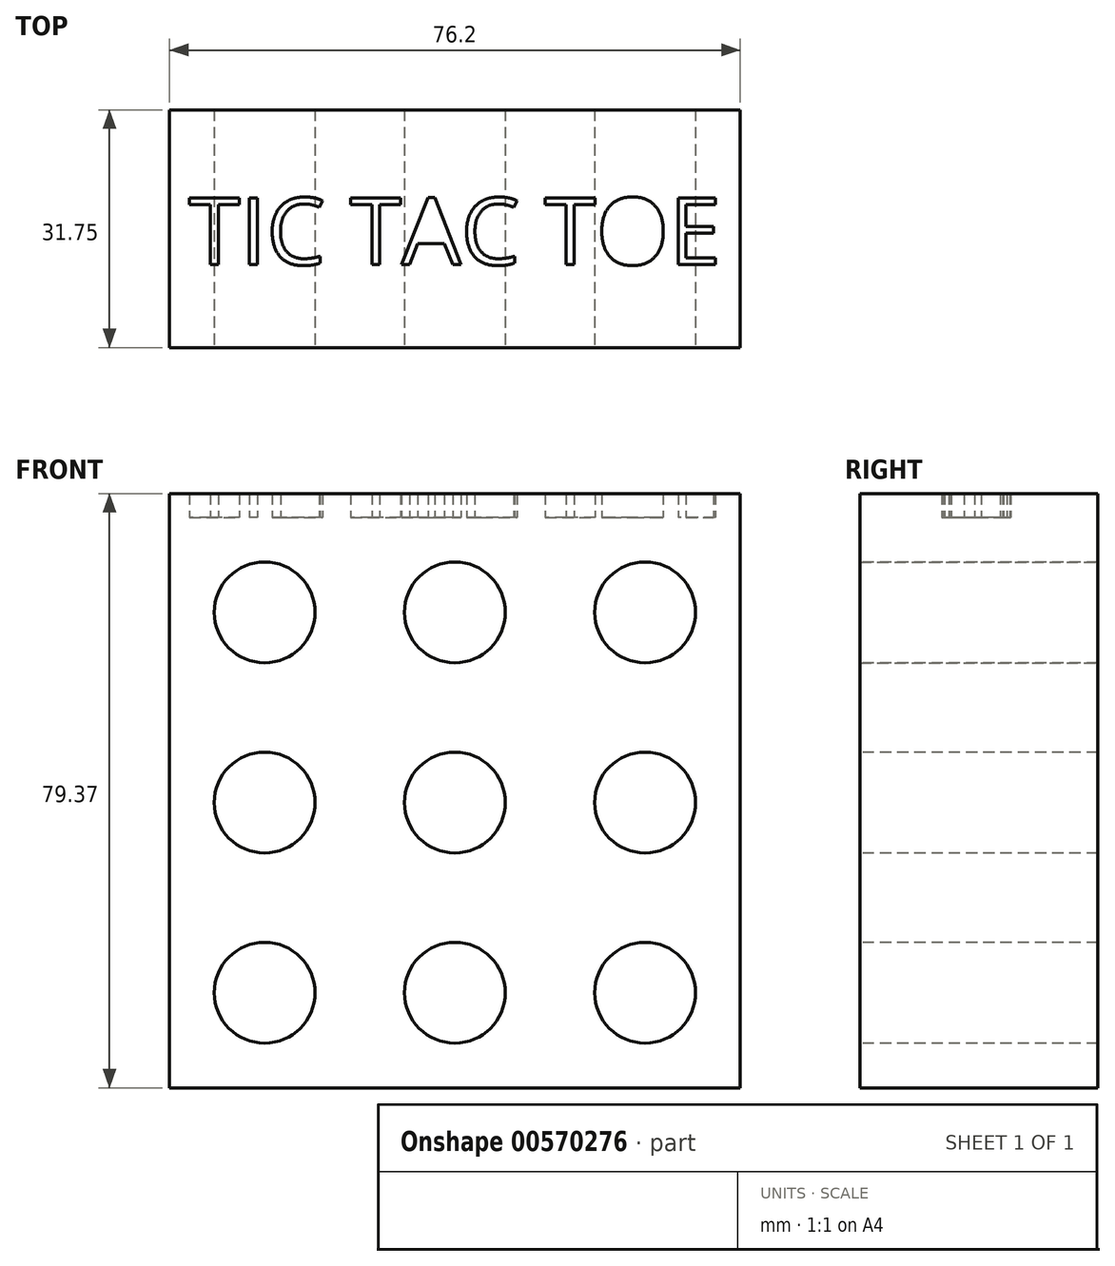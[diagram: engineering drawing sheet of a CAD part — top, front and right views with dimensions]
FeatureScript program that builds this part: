
annotation { "Feature Type Name" : "Feature", "Feature Type Description" : "" }
export const myFeature = defineFeature(function(context is Context, id is Id, definition is map)
    precondition{}
    {
        {
            var Q0;
            Q0=qCreatedBy(makeId("Front.planeOp"),FACE);
            var sketch = newSketch(context, id + "F0", { "sketchPlane" : qUnion([Q0])});
            skLineSegment(sketch, "E0.bottom", {"start": v(-47.47, 51.39) * mm, "end": v(28.73, 51.39) * mm});
            skLineSegment(sketch, "E0.top", {"start": v(-47.47, -24.81) * mm, "end": v(28.73, -24.81) * mm});
            skLineSegment(sketch, "E0.left", {"start": v(-47.47, 51.39) * mm, "end": v(-47.47, -24.81) * mm});
            skLineSegment(sketch, "E0.right", {"start": v(28.73, 51.39) * mm, "end": v(28.73, -24.81) * mm});
            skLineSegment(sketch, "E1", {"start": v(-9.37, 51.39) * mm, "end": v(-9.37, -24.81) * mm, "construction": true});
            skLineSegment(sketch, "E2", {"start": v(-47.47, 13.29) * mm, "end": v(28.73, 13.29) * mm, "construction": true});
            skSolve(sketch);
        }
        {
            var Q0;
            Q0=makeQuery(id+"F0.imprint","IMPRINT",FACE,{"disambiguationData":[TD([[makeQuery(id+"F0.imprint","IMPRINT",EDGE,{"derivedFrom":sQuery(id+"F0.wireOp",EDGE,"E0.bottom")}),-1.0]])]});
            extrude(context, id + "F1", {"entities" : qUnion([Q0]), "depth" : 31.75 * mm, "offsetDistance" : 25.4 * mm});
        }
        {
            var Q0;
            Q0=makeQuery(id+"F1.opExtrude","CAP_FACE",FACE,{"disambiguationData":[OSD([sQuery(id+"F0.wireOp",EDGE,"E0.bottom"),sQuery(id+"F0.wireOp",EDGE,"E0.top"),sQuery(id+"F0.wireOp",EDGE,"E0.left"),sQuery(id+"F0.wireOp",EDGE,"E0.right")])],"isStart":false});
            var sketch = newSketch(context, id + "F2", { "sketchPlane" : qUnion([Q0])});
            skCircle(sketch, "E3", {"center": v(-9.37, 13.29) * mm, "radius": 6.73 * mm});
            skSolve(sketch);
        }
        {
            var Q0;
            Q0=makeQuery(id+"F2.imprint","IMPRINT",FACE,{"disambiguationData":[TD([[makeQuery(id+"F2.imprint","IMPRINT",EDGE,{"derivedFrom":sQuery(id+"F2.wireOp",EDGE,"E3")}),1.0]])]});
            extrude(context, id + "F3", {"entities" : qUnion([Q0]), "operationType" : NewBodyOperationType.REMOVE, "oppositeDirection" : true, "depth" : 50.8 * mm, "offsetDistance" : 25.4 * mm});
        }
        {
            var Q0;
            Q0=makeQuery(id+"F1.opExtrude","CAP_FACE",FACE,{"disambiguationData":[OSD([sQuery(id+"F0.wireOp",EDGE,"E0.bottom"),sQuery(id+"F0.wireOp",EDGE,"E0.top"),sQuery(id+"F0.wireOp",EDGE,"E0.left"),sQuery(id+"F0.wireOp",EDGE,"E0.right")])],"isStart":false});
            var sketch = newSketch(context, id + "F4", { "sketchPlane" : qUnion([Q0])});
            skCircle(sketch, "E4", {"center": v(16.03, 38.69) * mm, "radius": 6.73 * mm});
            skSolve(sketch);
        }
        {
            var Q0;
            Q0=makeQuery(id+"F4.imprint","IMPRINT",FACE,{"disambiguationData":[TD([[makeQuery(id+"F4.imprint","IMPRINT",EDGE,{"derivedFrom":sQuery(id+"F4.wireOp",EDGE,"E4")}),-1.0]])]});
            var sketch = newSketch(context, id + "F5", { "sketchPlane" : qUnion([Q0])});
            skCircle(sketch, "E5", {"center": v(16.03, 13.29) * mm, "radius": 6.73 * mm});
            skSolve(sketch);
        }
        {
            var Q0;
            Q0=makeQuery(id+"F5.imprint","IMPRINT",FACE,{"disambiguationData":[TD([[makeQuery(id+"F5.imprint","IMPRINT",EDGE,{"derivedFrom":makeQuery(id+"F4.imprint","IMPRINT",EDGE,{"derivedFrom":sQuery(id+"F4.wireOp",EDGE,"E4")})}),1.0]])]});
            extrude(context, id + "F6", {"entities" : qUnion([Q0]), "operationType" : NewBodyOperationType.REMOVE, "oppositeDirection" : true, "depth" : 31.75 * mm, "offsetDistance" : 25.4 * mm});
        }
        {
            var Q0;
            Q0=makeQuery(id+"F5.imprint","IMPRINT",FACE,{"disambiguationData":[TD([[makeQuery(id+"F5.imprint","IMPRINT",EDGE,{"derivedFrom":sQuery(id+"F5.wireOp",EDGE,"E5")}),1.0]])]});
            extrude(context, id + "F7", {"entities" : qUnion([Q0]), "operationType" : NewBodyOperationType.REMOVE, "endBound" : BoundingType.THROUGH_ALL, "oppositeDirection" : true, "depth" : 25.4 * mm, "offsetDistance" : 25.4 * mm});
        }
        {
            var Q0;
            Q0=makeQuery(id+"F1.opExtrude","CAP_FACE",FACE,{"disambiguationData":[OSD([sQuery(id+"F0.wireOp",EDGE,"E0.bottom"),sQuery(id+"F0.wireOp",EDGE,"E0.top"),sQuery(id+"F0.wireOp",EDGE,"E0.left"),sQuery(id+"F0.wireOp",EDGE,"E0.right")])],"isStart":true});
            var sketch = newSketch(context, id + "F8", { "sketchPlane" : qUnion([Q0])});
            skCircle(sketch, "E6", {"center": v(9.37, 38.69) * mm, "radius": 6.73 * mm});
            skSolve(sketch);
        }
        {
            var Q0;
            Q0=makeQuery(id+"F8.imprint","IMPRINT",FACE,{"disambiguationData":[TD([[makeQuery(id+"F8.imprint","IMPRINT",EDGE,{"derivedFrom":sQuery(id+"F8.wireOp",EDGE,"E6")}),1.0]])]});
            extrude(context, id + "F9", {"entities" : qUnion([Q0]), "operationType" : NewBodyOperationType.REMOVE, "endBound" : BoundingType.THROUGH_ALL, "oppositeDirection" : true, "depth" : 25.4 * mm, "offsetDistance" : 25.4 * mm});
        }
        {
            var Q0;
            Q0=makeQuery(id+"F1.opExtrude","CAP_FACE",FACE,{"disambiguationData":[OSD([sQuery(id+"F0.wireOp",EDGE,"E0.bottom"),sQuery(id+"F0.wireOp",EDGE,"E0.top"),sQuery(id+"F0.wireOp",EDGE,"E0.left"),sQuery(id+"F0.wireOp",EDGE,"E0.right")])],"isStart":false});
            var sketch = newSketch(context, id + "F10", { "sketchPlane" : qUnion([Q0])});
            skCircle(sketch, "E7", {"center": v(-34.77, 38.69) * mm, "radius": 6.73 * mm});
            skSolve(sketch);
        }
        {
            var Q0;
            Q0=makeQuery(id+"F10.imprint","IMPRINT",FACE,{"disambiguationData":[TD([[makeQuery(id+"F10.imprint","IMPRINT",EDGE,{"derivedFrom":sQuery(id+"F10.wireOp",EDGE,"E7")}),1.0]])]});
            extrude(context, id + "F11", {"entities" : qUnion([Q0]), "operationType" : NewBodyOperationType.REMOVE, "endBound" : BoundingType.THROUGH_ALL, "oppositeDirection" : true, "depth" : 25.4 * mm, "offsetDistance" : 25.4 * mm});
        }
        {
            var Q0;
            Q0=makeQuery(id+"F1.opExtrude","CAP_FACE",FACE,{"disambiguationData":[OSD([sQuery(id+"F0.wireOp",EDGE,"E0.bottom"),sQuery(id+"F0.wireOp",EDGE,"E0.top"),sQuery(id+"F0.wireOp",EDGE,"E0.left"),sQuery(id+"F0.wireOp",EDGE,"E0.right")])],"isStart":false});
            var sketch = newSketch(context, id + "F12", { "sketchPlane" : qUnion([Q0])});
            skCircle(sketch, "E8", {"center": v(-34.77, 13.29) * mm, "radius": 6.73 * mm});
            skSolve(sketch);
        }
        {
            var Q0;
            Q0=makeQuery(id+"F12.imprint","IMPRINT",FACE,{"disambiguationData":[TD([[makeQuery(id+"F12.imprint","IMPRINT",EDGE,{"derivedFrom":sQuery(id+"F12.wireOp",EDGE,"E8")}),1.0]])]});
            extrude(context, id + "F13", {"entities" : qUnion([Q0]), "operationType" : NewBodyOperationType.REMOVE, "endBound" : BoundingType.THROUGH_ALL, "oppositeDirection" : true, "depth" : 25.4 * mm, "offsetDistance" : 25.4 * mm});
        }
        {
            var Q0;
            Q0=makeQuery(id+"F1.opExtrude","CAP_FACE",FACE,{"disambiguationData":[OSD([sQuery(id+"F0.wireOp",EDGE,"E0.bottom"),sQuery(id+"F0.wireOp",EDGE,"E0.top"),sQuery(id+"F0.wireOp",EDGE,"E0.left"),sQuery(id+"F0.wireOp",EDGE,"E0.right")])],"isStart":false});
            var sketch = newSketch(context, id + "F14", { "sketchPlane" : qUnion([Q0])});
            skCircle(sketch, "E9", {"center": v(-34.77, -12.11) * mm, "radius": 6.73 * mm});
            skSolve(sketch);
        }
        {
            var Q0;
            Q0=makeQuery(id+"F14.imprint","IMPRINT",FACE,{"disambiguationData":[TD([[makeQuery(id+"F14.imprint","IMPRINT",EDGE,{"derivedFrom":sQuery(id+"F14.wireOp",EDGE,"E9")}),1.0]])]});
            extrude(context, id + "F15", {"entities" : qUnion([Q0]), "operationType" : NewBodyOperationType.REMOVE, "endBound" : BoundingType.THROUGH_ALL, "oppositeDirection" : true, "depth" : 25.4 * mm, "offsetDistance" : 25.4 * mm});
        }
        {
            var Q0;
            Q0=makeQuery(id+"F1.opExtrude","CAP_FACE",FACE,{"disambiguationData":[OSD([sQuery(id+"F0.wireOp",EDGE,"E0.bottom"),sQuery(id+"F0.wireOp",EDGE,"E0.top"),sQuery(id+"F0.wireOp",EDGE,"E0.left"),sQuery(id+"F0.wireOp",EDGE,"E0.right")])],"isStart":false});
            var sketch = newSketch(context, id + "F16", { "sketchPlane" : qUnion([Q0])});
            skCircle(sketch, "E10", {"center": v(-9.37, -12.11) * mm, "radius": 6.73 * mm});
            skSolve(sketch);
        }
        {
            var Q0;
            Q0=makeQuery(id+"F16.imprint","IMPRINT",FACE,{"disambiguationData":[TD([[makeQuery(id+"F16.imprint","IMPRINT",EDGE,{"derivedFrom":sQuery(id+"F16.wireOp",EDGE,"E10")}),1.0]])]});
            extrude(context, id + "F17", {"entities" : qUnion([Q0]), "operationType" : NewBodyOperationType.REMOVE, "endBound" : BoundingType.THROUGH_ALL, "oppositeDirection" : true, "depth" : 25.4 * mm, "offsetDistance" : 25.4 * mm});
        }
        {
            var Q0;
            Q0=makeQuery(id+"F1.opExtrude","CAP_FACE",FACE,{"disambiguationData":[OSD([sQuery(id+"F0.wireOp",EDGE,"E0.bottom"),sQuery(id+"F0.wireOp",EDGE,"E0.top"),sQuery(id+"F0.wireOp",EDGE,"E0.left"),sQuery(id+"F0.wireOp",EDGE,"E0.right")])],"isStart":false});
            var sketch = newSketch(context, id + "F18", { "sketchPlane" : qUnion([Q0])});
            skCircle(sketch, "E11", {"center": v(16.03, -12.11) * mm, "radius": 6.73 * mm});
            skSolve(sketch);
        }
        {
            var Q0;
            Q0=makeQuery(id+"F18.imprint","IMPRINT",FACE,{"disambiguationData":[TD([[makeQuery(id+"F18.imprint","IMPRINT",EDGE,{"derivedFrom":sQuery(id+"F18.wireOp",EDGE,"E11")}),1.0]])]});
            extrude(context, id + "F19", {"entities" : qUnion([Q0]), "operationType" : NewBodyOperationType.REMOVE, "endBound" : BoundingType.THROUGH_ALL, "oppositeDirection" : true, "depth" : 25.4 * mm, "offsetDistance" : 25.4 * mm});
        }
        {
            var Q0;
            Q0=makeQuery(id+"F1.opExtrude","SWEPT_FACE",FACE,{"disambiguationData":[OSD([sQuery(id+"F0.wireOp",EDGE,"E0.bottom")])]});
            var sketch = newSketch(context, id + "F20", { "sketchPlane" : qUnion([Q0])});
            skText(sketch, "E12", { "text": "TIC TAC TOE ", "fontName": "OpenSans-Regular.ttf"});
            const initialGuessF20  = {"E12": [-0.04493, -0.02069, 1, 0, 0.009]};
            skSetInitialGuess(sketch, initialGuessF20);
            skSolve(sketch);
        }
        {
            var Q0;
            Q0=makeQuery(id+"F20.imprint","IMPRINT",FACE,{"disambiguationData":[TD([[makeQuery(id+"F20.imprint","IMPRINT",EDGE,{"derivedFrom":sQuery(id+"F20.wireOp",EDGE,"E12.sketch_text.stroke-0")}),1.0]])]});
            extrude(context, id + "F21", {"entities" : qUnion([Q0]), "operationType" : NewBodyOperationType.ADD, "depth" : 3.17 * mm, "offsetDistance" : 25.4 * mm});
        }
    });
